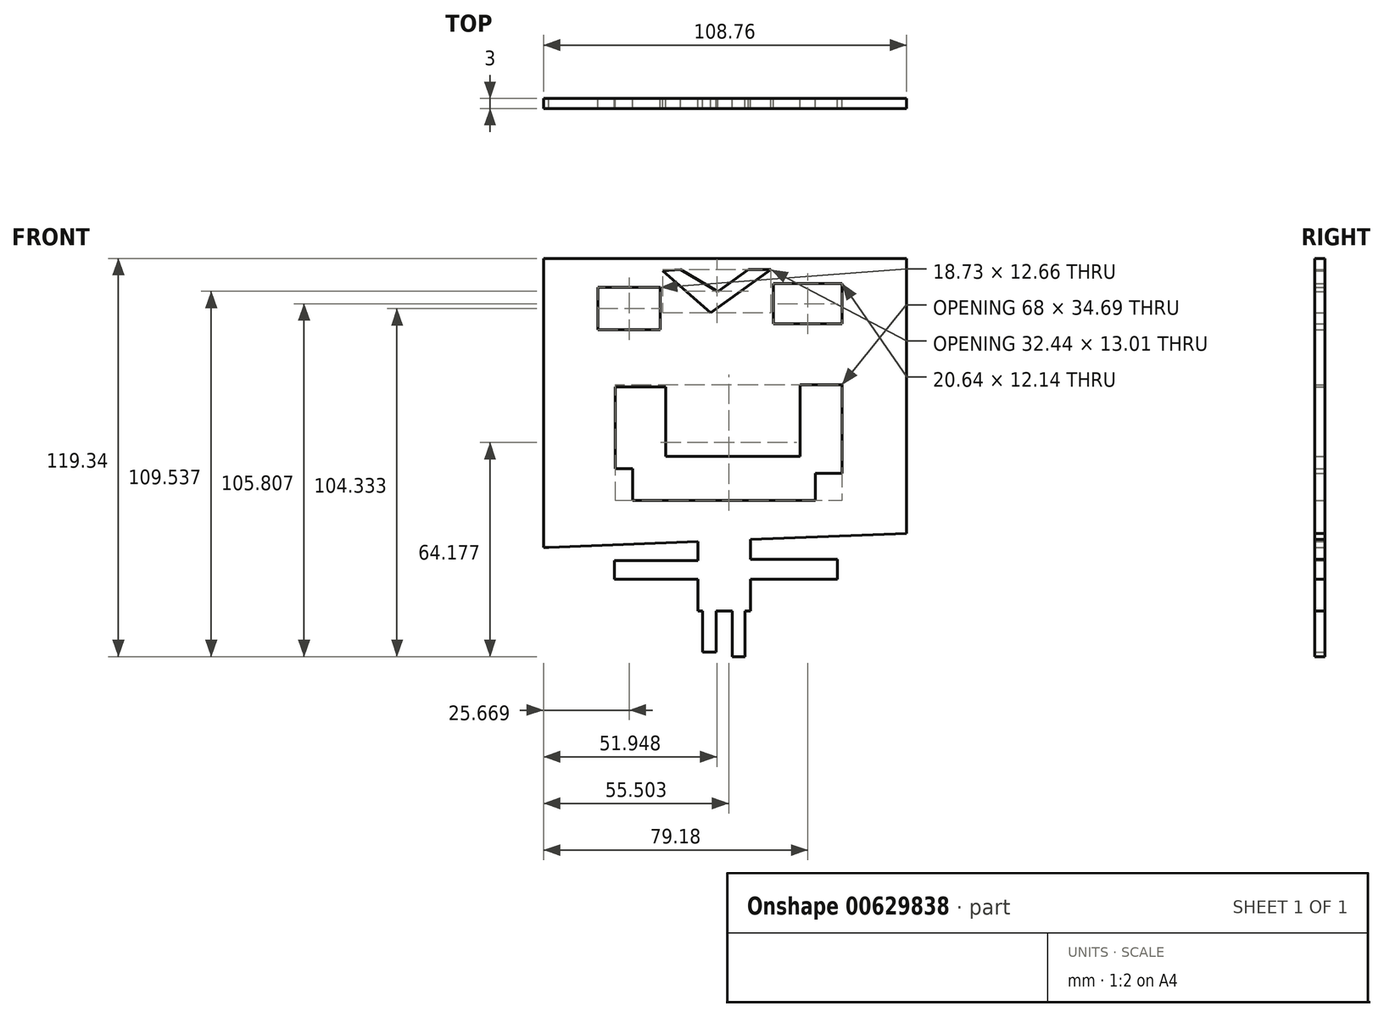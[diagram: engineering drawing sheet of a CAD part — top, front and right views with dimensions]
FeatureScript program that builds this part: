
annotation { "Feature Type Name" : "Feature", "Feature Type Description" : "" }
export const myFeature = defineFeature(function(context is Context, id is Id, definition is map)
    precondition{}
    {
        {
            var Q0;
            Q0=qCreatedBy(makeId("Front.planeOp"),FACE);
            var sketch = newSketch(context, id + "F0", { "sketchPlane" : qUnion([Q0])});
            skLineSegment(sketch, "E0", {"start": v(-55.33, -39.8) * mm, "end": v(-55.33, 46.75) * mm});
            skLineSegment(sketch, "E1", {"start": v(-55.33, 46.75) * mm, "end": v(53.43, 46.75) * mm});
            skLineSegment(sketch, "E2", {"start": v(53.43, 46.75) * mm, "end": v(53.43, -35.65) * mm});
            skLineSegment(sketch, "E3", {"start": v(53.43, -35.65) * mm, "end": v(-53.77, -39.8) * mm});
            skLineSegment(sketch, "E4", {"start": v(-53.77, -39.8) * mm, "end": v(-55.33, -39.8) * mm});
            skLineSegment(sketch, "E5.bottom", {"start": v(-39.03, 38.07) * mm, "end": v(-20.3, 38.07) * mm});
            skLineSegment(sketch, "E5.top", {"start": v(-39.03, 25.41) * mm, "end": v(-20.3, 25.41) * mm});
            skLineSegment(sketch, "E5.left", {"start": v(-39.03, 38.07) * mm, "end": v(-39.03, 25.41) * mm});
            skLineSegment(sketch, "E5.right", {"start": v(-20.3, 38.07) * mm, "end": v(-20.3, 25.41) * mm});
            skLineSegment(sketch, "E6.bottom", {"start": v(13.53, 27.15) * mm, "end": v(34.17, 27.15) * mm});
            skLineSegment(sketch, "E6.top", {"start": v(13.53, 39.29) * mm, "end": v(34.17, 39.29) * mm});
            skLineSegment(sketch, "E6.left", {"start": v(13.53, 27.15) * mm, "end": v(13.53, 39.29) * mm});
            skLineSegment(sketch, "E6.right", {"start": v(34.17, 27.15) * mm, "end": v(34.17, 39.29) * mm});
            skLineSegment(sketch, "E7.bottom", {"start": v(-33.82, 8.24) * mm, "end": v(-18.73, 8.24) * mm});
            skLineSegment(sketch, "E7.top", {"start": v(-33.82, -16.22) * mm, "end": v(-18.73, -16.22) * mm});
            skLineSegment(sketch, "E7.left", {"start": v(-33.82, 8.24) * mm, "end": v(-33.82, -16.22) * mm});
            skLineSegment(sketch, "E7.right", {"start": v(-18.73, 8.24) * mm, "end": v(-18.73, -16.22) * mm});
            skLineSegment(sketch, "E8.bottom", {"start": v(-28.62, -12.58) * mm, "end": v(26.2, -12.58) * mm});
            skLineSegment(sketch, "E8.top", {"start": v(-28.62, -25.76) * mm, "end": v(26.2, -25.76) * mm});
            skLineSegment(sketch, "E8.left", {"start": v(-28.62, -12.58) * mm, "end": v(-28.62, -25.76) * mm});
            skLineSegment(sketch, "E8.right", {"start": v(26.2, -12.58) * mm, "end": v(26.2, -25.76) * mm});
            skLineSegment(sketch, "E9.bottom", {"start": v(21.5, -17.6) * mm, "end": v(34.17, -17.6) * mm});
            skLineSegment(sketch, "E9.top", {"start": v(21.5, 8.93) * mm, "end": v(34.17, 8.93) * mm});
            skLineSegment(sketch, "E9.left", {"start": v(21.5, -17.6) * mm, "end": v(21.5, 8.93) * mm});
            skLineSegment(sketch, "E9.right", {"start": v(34.17, -17.6) * mm, "end": v(34.17, 8.93) * mm});
            skLineSegment(sketch, "E10", {"start": v(-19.6, 43.1) * mm, "end": v(-5.2, 30.44) * mm});
            skLineSegment(sketch, "E11", {"start": v(-5.2, 30.44) * mm, "end": v(12.84, 43.45) * mm});
            skLineSegment(sketch, "E12", {"start": v(12.84, 43.45) * mm, "end": v(6.07, 43.45) * mm});
            skLineSegment(sketch, "E13", {"start": v(6.07, 43.45) * mm, "end": v(-3.07, 36.86) * mm});
            skLineSegment(sketch, "E14", {"start": v(-3.07, 36.86) * mm, "end": v(-14.22, 43.45) * mm});
            skLineSegment(sketch, "E15", {"start": v(-14.22, 43.45) * mm, "end": v(-19.6, 43.1) * mm});
            skLineSegment(sketch, "E16.bottom", {"start": v(-9.02, -34.78) * mm, "end": v(6.76, -34.78) * mm});
            skLineSegment(sketch, "E16.top", {"start": v(-9.02, -58.89) * mm, "end": v(6.76, -58.89) * mm});
            skLineSegment(sketch, "E16.left", {"start": v(-9.02, -34.78) * mm, "end": v(-9.02, -58.89) * mm});
            skLineSegment(sketch, "E16.right", {"start": v(6.76, -34.78) * mm, "end": v(6.76, -58.89) * mm});
            skLineSegment(sketch, "E17.bottom", {"start": v(2.95, -49.35) * mm, "end": v(32.78, -49.35) * mm});
            skLineSegment(sketch, "E17.top", {"start": v(2.95, -43.45) * mm, "end": v(32.78, -43.45) * mm});
            skLineSegment(sketch, "E17.left", {"start": v(2.95, -49.35) * mm, "end": v(2.95, -43.45) * mm});
            skLineSegment(sketch, "E17.right", {"start": v(32.78, -49.35) * mm, "end": v(32.78, -43.45) * mm});
            skLineSegment(sketch, "E18.bottom", {"start": v(-6.76, -49.35) * mm, "end": v(-34, -49.35) * mm});
            skLineSegment(sketch, "E18.top", {"start": v(-6.76, -43.8) * mm, "end": v(-34, -43.8) * mm});
            skLineSegment(sketch, "E18.left", {"start": v(-6.76, -49.35) * mm, "end": v(-6.76, -43.8) * mm});
            skLineSegment(sketch, "E18.right", {"start": v(-34, -49.35) * mm, "end": v(-34, -43.8) * mm});
            skLineSegment(sketch, "E19.bottom", {"start": v(-7.63, -55.77) * mm, "end": v(-3.64, -55.77) * mm});
            skLineSegment(sketch, "E19.top", {"start": v(-7.63, -71.2) * mm, "end": v(-3.64, -71.2) * mm});
            skLineSegment(sketch, "E19.left", {"start": v(-7.63, -55.77) * mm, "end": v(-7.63, -71.2) * mm});
            skLineSegment(sketch, "E19.right", {"start": v(-3.64, -55.77) * mm, "end": v(-3.64, -71.2) * mm});
            skLineSegment(sketch, "E20.bottom", {"start": v(1.21, -56.63) * mm, "end": v(5.03, -56.63) * mm});
            skLineSegment(sketch, "E20.top", {"start": v(1.21, -72.6) * mm, "end": v(5.03, -72.6) * mm});
            skLineSegment(sketch, "E20.left", {"start": v(1.21, -56.63) * mm, "end": v(1.21, -72.6) * mm});
            skLineSegment(sketch, "E20.right", {"start": v(5.03, -56.63) * mm, "end": v(5.03, -72.6) * mm});
            skSolve(sketch);
        }
        {
            var Q0;
            {var subQ5=sQuery(id+"F0.wireOp",EDGE,"E19.top");Q0=makeQuery(id+"F0.imprint","IMPRINT",FACE,{"disambiguationData":[TD([[makeQuery(id+"F0.imprint","IMPRINT",EDGE,{"derivedFrom":subQ5}),1.0]])]});}
            var Q1;
            {var subQ5=sQuery(id+"F0.wireOp",EDGE,"E20.top");Q1=makeQuery(id+"F0.imprint","IMPRINT",FACE,{"disambiguationData":[TD([[makeQuery(id+"F0.imprint","IMPRINT",EDGE,{"derivedFrom":subQ5}),1.0]])]});}
            var Q2;
            {var subQ5=sQuery(id+"F0.wireOp",EDGE,"E18.right");Q2=makeQuery(id+"F0.imprint","IMPRINT",FACE,{"disambiguationData":[TD([[makeQuery(id+"F0.imprint","IMPRINT",EDGE,{"derivedFrom":subQ5}),-1.0]])]});}
            var Q3;
            {var subQ5=sQuery(id+"F0.wireOp",EDGE,"E17.right");Q3=makeQuery(id+"F0.imprint","IMPRINT",FACE,{"disambiguationData":[TD([[makeQuery(id+"F0.imprint","IMPRINT",EDGE,{"derivedFrom":subQ5}),1.0]])]});}
            var Q4;
            {var subQ5=sQuery(id+"F0.wireOp",EDGE,"E16.bottom");Q4=makeQuery(id+"F0.imprint","IMPRINT",FACE,{"disambiguationData":[TD([[makeQuery(id+"F0.imprint","IMPRINT",EDGE,{"derivedFrom":subQ5}),-1.0]])]});}
            var Q5;
            {var subQ5=sQuery(id+"F0.wireOp",EDGE,"E19.bottom");Q5=makeQuery(id+"F0.imprint","IMPRINT",FACE,{"disambiguationData":[TD([[makeQuery(id+"F0.imprint","IMPRINT",EDGE,{"derivedFrom":subQ5}),-1.0]])]});}
            var Q6;
            {var subQ5=sQuery(id+"F0.wireOp",EDGE,"E20.bottom");Q6=makeQuery(id+"F0.imprint","IMPRINT",FACE,{"disambiguationData":[TD([[makeQuery(id+"F0.imprint","IMPRINT",EDGE,{"derivedFrom":subQ5}),-1.0]])]});}
            var Q7;
            {var subQ5=sQuery(id+"F0.wireOp",EDGE,"E18.left");Q7=makeQuery(id+"F0.imprint","IMPRINT",FACE,{"disambiguationData":[TD([[makeQuery(id+"F0.imprint","IMPRINT",EDGE,{"derivedFrom":subQ5}),1.0]])]});}
            var Q8;
            {var subQ5=sQuery(id+"F0.wireOp",EDGE,"E17.left");Q8=makeQuery(id+"F0.imprint","IMPRINT",FACE,{"disambiguationData":[TD([[makeQuery(id+"F0.imprint","IMPRINT",EDGE,{"derivedFrom":subQ5}),-1.0]])]});}
            var Q9;
            {var subQ24=sQuery(id+"F0.wireOp",EDGE,"E17.left");Q9=makeQuery(id+"F0.imprint","IMPRINT",FACE,{"disambiguationData":[TD([[makeQuery(id+"F0.imprint","IMPRINT",EDGE,{"derivedFrom":subQ24}),1.0]])]});}
            var Q10;
            Q10=makeQuery(id+"F0.imprint","IMPRINT",FACE,{"disambiguationData":[TD([[makeQuery(id+"F0.imprint","IMPRINT",EDGE,{"derivedFrom":sQuery(id+"F0.wireOp",EDGE,"E0")}),-1.0]])]});
            extrude(context, id + "F1", {"entities" : qUnion([Q0, Q1, Q2, Q3, Q4, Q5, Q6, Q7, Q8, Q9, Q10]), "depth" : 3 * mm, "offsetDistance" : 25 * mm});
        }
    });
